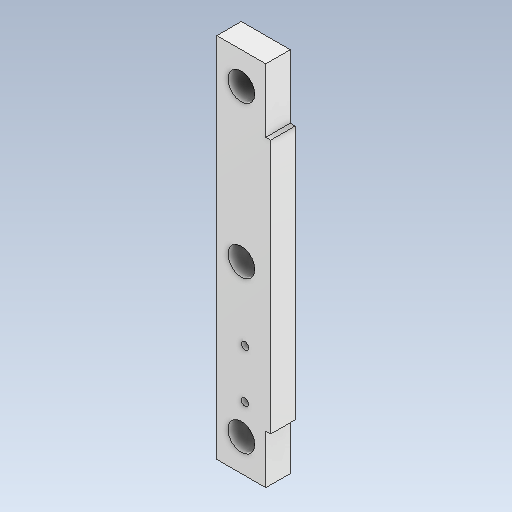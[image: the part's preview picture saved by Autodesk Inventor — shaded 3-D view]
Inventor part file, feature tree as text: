
AUTODESK INVENTOR PART (.ipt)
format: ipt  version: 2020 (Build 240168000, 168)  size: 150,016 bytes
history: native  units: mm
features: other x1, sketch x1, extrude x1
ambient origin geometry x8: Origin, YZ Plane, XZ Plane, XY Plane, X Axis, Y Axis, Z Axis, Center Point
bodies: Body1 (feature_tree)
feature tree (3):
  other  "Bryła1"
  sketch  "Szkic1"
  extrude  "Wyciągnięcie proste1"  Depth=75.0mm
